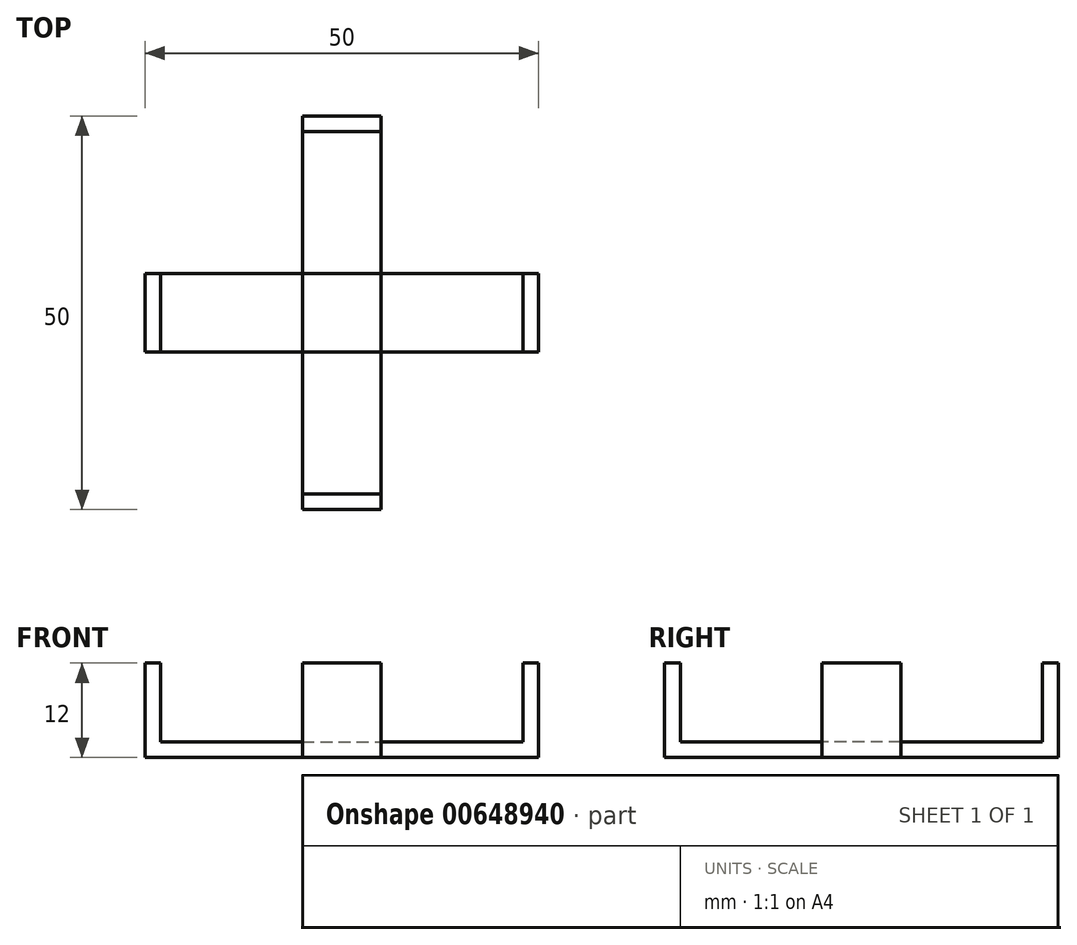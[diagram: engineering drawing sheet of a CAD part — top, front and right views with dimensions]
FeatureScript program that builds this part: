
annotation { "Feature Type Name" : "Feature", "Feature Type Description" : "" }
export const myFeature = defineFeature(function(context is Context, id is Id, definition is map)
    precondition{}
    {
        {
            var Q0;
            Q0=qCreatedBy(makeId("Top.planeOp"),FACE);
            var sketch = newSketch(context, id + "F0", { "sketchPlane" : qUnion([Q0])});
            skLineSegment(sketch, "E0.bottom", {"start": v(150, 80) * mm, "end": v(-150, 80) * mm});
            skLineSegment(sketch, "E0.top", {"start": v(150, -80) * mm, "end": v(-150, -80) * mm});
            skLineSegment(sketch, "E0.left", {"start": v(150, 80) * mm, "end": v(150, -80) * mm});
            skLineSegment(sketch, "E0.right", {"start": v(-150, 80) * mm, "end": v(-150, -80) * mm});
            skPoint(sketch, "E0.middle", {"position": v(0, 0) * mm});
            skSolve(sketch);
        }
        {
            var Q0;
            Q0 = qSketchRegion(id + "F0", true);
            extrude(context, id + "F1", {"entities" : qUnion([Q0]), "depth" : 2 * mm, "offsetDistance" : 25 * mm});
        }
        {
            var Q0;
            Q0=makeQuery(id+"F1.opExtrude","CAP_FACE",FACE,{"disambiguationData":[OSD([sQuery(id+"F0.wireOp",EDGE,"E0.bottom"),sQuery(id+"F0.wireOp",EDGE,"E0.top"),sQuery(id+"F0.wireOp",EDGE,"E0.left"),sQuery(id+"F0.wireOp",EDGE,"E0.right")])],"isStart":false});
            var sketch = newSketch(context, id + "F2", { "sketchPlane" : qUnion([Q0])});
            skLineSegment(sketch, "E1.bottom", {"start": v(5, 5) * mm, "end": v(-5, 5) * mm, "construction": true});
            skLineSegment(sketch, "E1.top", {"start": v(5, -5) * mm, "end": v(-5, -5) * mm, "construction": true});
            skLineSegment(sketch, "E1.left", {"start": v(5, 5) * mm, "end": v(5, -5) * mm, "construction": true});
            skLineSegment(sketch, "E1.right", {"start": v(-5, 5) * mm, "end": v(-5, -5) * mm, "construction": true});
            skPoint(sketch, "E1.middle", {"position": v(0, 0) * mm});
            skLineSegment(sketch, "E2.bottom", {"start": v(-5, 5) * mm, "end": v(5, 5) * mm, "construction": true});
            skLineSegment(sketch, "E2.top", {"start": v(-5, 5) * mm, "end": v(5, 5) * mm, "construction": true});
            skLineSegment(sketch, "E2.left", {"start": v(-5, 5) * mm, "end": v(-5, 5) * mm});
            skLineSegment(sketch, "E2.right", {"start": v(5, 5) * mm, "end": v(5, 5) * mm});
            skLineSegment(sketch, "E3.bottom", {"start": v(-5, 5) * mm, "end": v(5, 5) * mm});
            skLineSegment(sketch, "E3.top", {"start": v(-5, 25) * mm, "end": v(5, 25) * mm});
            skLineSegment(sketch, "E3.left", {"start": v(-5, 5) * mm, "end": v(-5, 25) * mm});
            skLineSegment(sketch, "E3.right", {"start": v(5, 5) * mm, "end": v(5, 25) * mm});
            skLineSegment(sketch, "E4.bottom", {"start": v(5, 5) * mm, "end": v(25, 5) * mm});
            skLineSegment(sketch, "E4.top", {"start": v(5, -5) * mm, "end": v(25, -5) * mm});
            skLineSegment(sketch, "E4.left", {"start": v(5, 5) * mm, "end": v(5, -5) * mm});
            skLineSegment(sketch, "E4.right", {"start": v(25, 5) * mm, "end": v(25, -5) * mm});
            skLineSegment(sketch, "E5.bottom", {"start": v(5, -5) * mm, "end": v(-5, -5) * mm});
            skLineSegment(sketch, "E5.top", {"start": v(5, -25) * mm, "end": v(-5, -25) * mm});
            skLineSegment(sketch, "E5.left", {"start": v(5, -5) * mm, "end": v(5, -25) * mm});
            skLineSegment(sketch, "E5.right", {"start": v(-5, -5) * mm, "end": v(-5, -25) * mm});
            skLineSegment(sketch, "E6.bottom", {"start": v(-5, 5) * mm, "end": v(-25, 5) * mm});
            skLineSegment(sketch, "E6.top", {"start": v(-5, -5) * mm, "end": v(-25, -5) * mm});
            skLineSegment(sketch, "E6.left", {"start": v(-5, 5) * mm, "end": v(-5, -5) * mm});
            skLineSegment(sketch, "E6.right", {"start": v(-25, 5) * mm, "end": v(-25, -5) * mm});
            skSolve(sketch);
        }
        {
            var Q0;
            Q0=makeQuery(id+"F2.imprint","IMPRINT",FACE,{"disambiguationData":[TD([[makeQuery(id+"F2.imprint","IMPRINT",EDGE,{"derivedFrom":sQuery(id+"F2.wireOp",EDGE,"E3.bottom")}),1.0]])]});
            var Q1;
            Q1=makeQuery(id+"F2.imprint","IMPRINT",FACE,{"disambiguationData":[TD([[makeQuery(id+"F2.imprint","IMPRINT",EDGE,{"derivedFrom":sQuery(id+"F2.wireOp",EDGE,"E6.bottom")}),1.0]])]});
            var Q2;
            Q2=makeQuery(id+"F2.imprint","IMPRINT",FACE,{"disambiguationData":[TD([[makeQuery(id+"F2.imprint","IMPRINT",EDGE,{"derivedFrom":sQuery(id+"F2.wireOp",EDGE,"E5.bottom")}),1.0]])]});
            var Q3;
            Q3=makeQuery(id+"F2.imprint","IMPRINT",FACE,{"disambiguationData":[TD([[makeQuery(id+"F2.imprint","IMPRINT",EDGE,{"derivedFrom":sQuery(id+"F2.wireOp",EDGE,"E4.bottom")}),-1.0]])]});
            extrude(context, id + "F3", {"entities" : qUnion([Q0, Q1, Q2, Q3]), "depth" : 2 * mm, "offsetDistance" : 25 * mm});
        }
        {
            var Q0;
            Q0=makeQuery(id+"F3.opExtrude","CAP_FACE",FACE,{"disambiguationData":[OSD([sQuery(id+"F2.wireOp",EDGE,"E3.bottom"),sQuery(id+"F2.wireOp",EDGE,"E3.top"),sQuery(id+"F2.wireOp",EDGE,"E3.left"),sQuery(id+"F2.wireOp",EDGE,"E3.right")])],"isStart":false});
            var sketch = newSketch(context, id + "F4", { "sketchPlane" : qUnion([Q0])});
            skLineSegment(sketch, "E7.bottom", {"start": v(-5, 25) * mm, "end": v(5, 25) * mm});
            skLineSegment(sketch, "E7.top", {"start": v(-5, 23) * mm, "end": v(5, 23) * mm});
            skLineSegment(sketch, "E7.left", {"start": v(-5, 25) * mm, "end": v(-5, 23) * mm});
            skLineSegment(sketch, "E7.right", {"start": v(5, 25) * mm, "end": v(5, 23) * mm});
            skSolve(sketch);
        }
        {
            var Q0;
            Q0 = qSketchRegion(id + "F4", true);
            extrude(context, id + "F5", {"entities" : qUnion([Q0]), "operationType" : NewBodyOperationType.ADD, "depth" : 10 * mm, "offsetDistance" : 25 * mm});
        }
        {
            var Q0;
            Q0=makeQuery(id+"F3.opExtrude","CAP_FACE",FACE,{"disambiguationData":[OSD([sQuery(id+"F2.wireOp",EDGE,"E6.bottom"),sQuery(id+"F2.wireOp",EDGE,"E6.top"),sQuery(id+"F2.wireOp",EDGE,"E6.left"),sQuery(id+"F2.wireOp",EDGE,"E6.right")])],"isStart":false});
            var sketch = newSketch(context, id + "F6", { "sketchPlane" : qUnion([Q0])});
            skLineSegment(sketch, "E8.bottom", {"start": v(-25, 5) * mm, "end": v(-23, 5) * mm});
            skLineSegment(sketch, "E8.top", {"start": v(-25, -5) * mm, "end": v(-23, -5) * mm});
            skLineSegment(sketch, "E8.left", {"start": v(-25, 5) * mm, "end": v(-25, -5) * mm});
            skLineSegment(sketch, "E8.right", {"start": v(-23, 5) * mm, "end": v(-23, -5) * mm});
            skSolve(sketch);
        }
        {
            var Q0;
            Q0 = qSketchRegion(id + "F6", true);
            extrude(context, id + "F7", {"entities" : qUnion([Q0]), "operationType" : NewBodyOperationType.ADD, "depth" : 10 * mm, "offsetDistance" : 25 * mm});
        }
        {
            var Q0;
            Q0=makeQuery(id+"F3.opExtrude","CAP_FACE",FACE,{"disambiguationData":[OSD([sQuery(id+"F2.wireOp",EDGE,"E4.bottom"),sQuery(id+"F2.wireOp",EDGE,"E4.top"),sQuery(id+"F2.wireOp",EDGE,"E4.left"),sQuery(id+"F2.wireOp",EDGE,"E4.right")])],"isStart":false});
            var sketch = newSketch(context, id + "F8", { "sketchPlane" : qUnion([Q0])});
            skLineSegment(sketch, "E9.bottom", {"start": v(25, 5) * mm, "end": v(23, 5) * mm});
            skLineSegment(sketch, "E9.top", {"start": v(25, -5) * mm, "end": v(23, -5) * mm});
            skLineSegment(sketch, "E9.left", {"start": v(25, 5) * mm, "end": v(25, -5) * mm});
            skLineSegment(sketch, "E9.right", {"start": v(23, 5) * mm, "end": v(23, -5) * mm});
            skSolve(sketch);
        }
        {
            var Q0;
            Q0 = qSketchRegion(id + "F8", true);
            extrude(context, id + "F9", {"entities" : qUnion([Q0]), "operationType" : NewBodyOperationType.ADD, "depth" : 10 * mm, "offsetDistance" : 25 * mm});
        }
        {
            var Q0;
            Q0=makeQuery(id+"F3.opExtrude","CAP_FACE",FACE,{"disambiguationData":[OSD([sQuery(id+"F2.wireOp",EDGE,"E5.bottom"),sQuery(id+"F2.wireOp",EDGE,"E5.top"),sQuery(id+"F2.wireOp",EDGE,"E5.left"),sQuery(id+"F2.wireOp",EDGE,"E5.right")])],"isStart":false});
            var sketch = newSketch(context, id + "F10", { "sketchPlane" : qUnion([Q0])});
            skLineSegment(sketch, "E10.bottom", {"start": v(-5, -25) * mm, "end": v(5, -25) * mm});
            skLineSegment(sketch, "E10.top", {"start": v(-5, -23) * mm, "end": v(5, -23) * mm});
            skLineSegment(sketch, "E10.left", {"start": v(-5, -25) * mm, "end": v(-5, -23) * mm});
            skLineSegment(sketch, "E10.right", {"start": v(5, -25) * mm, "end": v(5, -23) * mm});
            skSolve(sketch);
        }
        {
            var Q0;
            Q0 = qSketchRegion(id + "F10", true);
            extrude(context, id + "F11", {"entities" : qUnion([Q0]), "operationType" : NewBodyOperationType.ADD, "depth" : 10 * mm, "offsetDistance" : 25 * mm});
        }
        {
            var Q0;
            Q0=makeQuery(id+"F1.opExtrude","SWEPT_BODY",BODY,{"disambiguationData":[OSD([sQuery(id+"F0.wireOp",EDGE,"E0.bottom"),sQuery(id+"F0.wireOp",EDGE,"E0.top"),sQuery(id+"F0.wireOp",EDGE,"E0.left"),sQuery(id+"F0.wireOp",EDGE,"E0.right")])]});
            deleteBodies(context, id + "F12", {"entities" : qUnion([Q0])});
        }
    });
